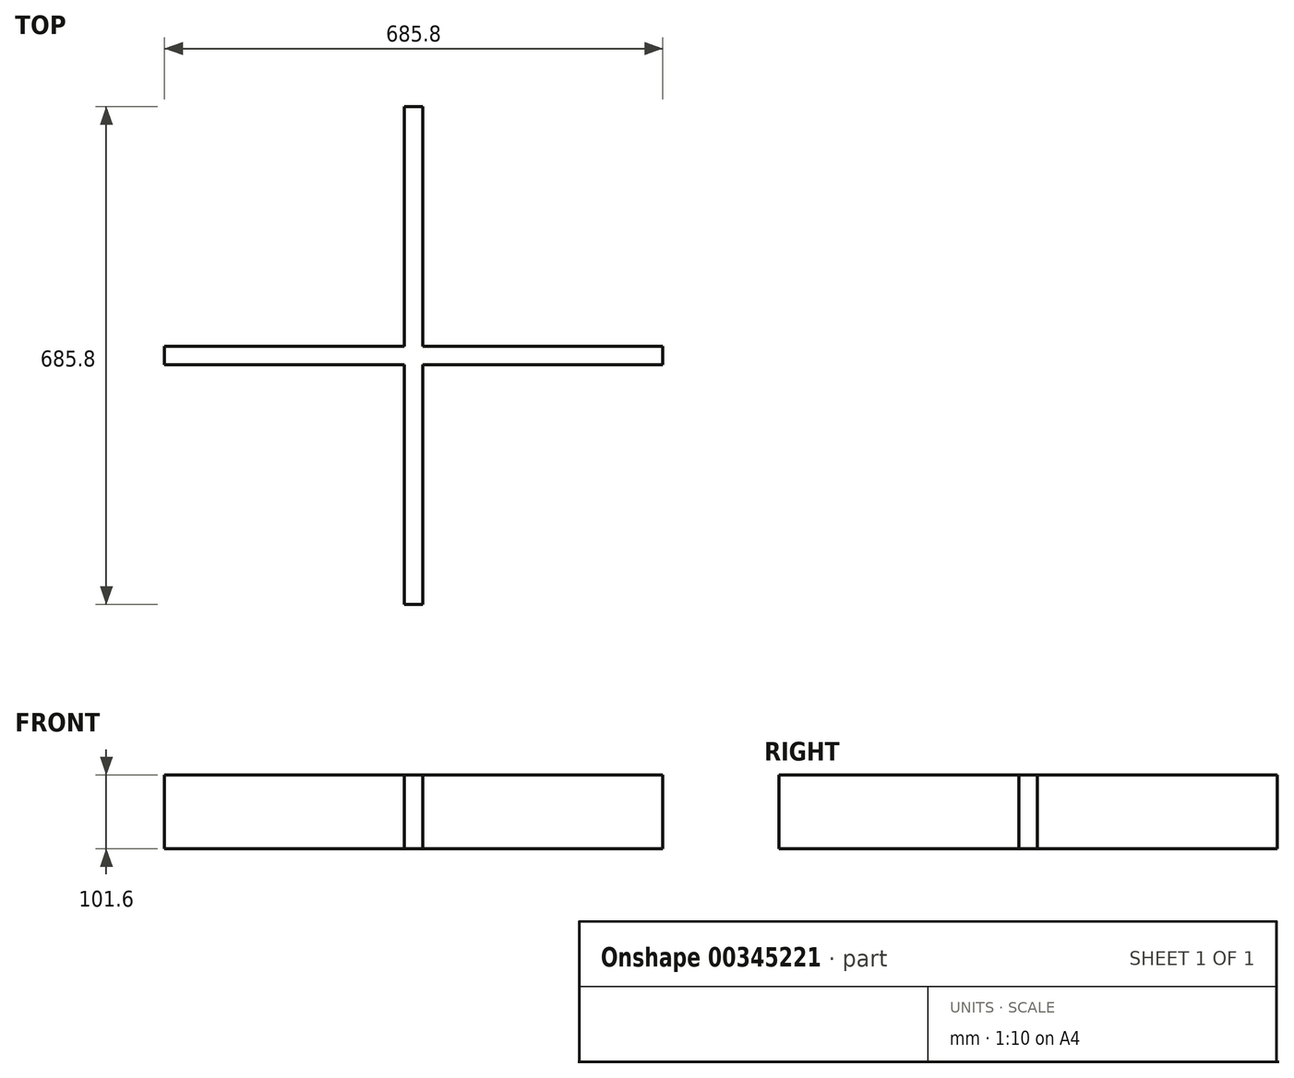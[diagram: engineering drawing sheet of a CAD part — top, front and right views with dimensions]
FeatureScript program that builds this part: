
annotation { "Feature Type Name" : "Feature", "Feature Type Description" : "" }
export const myFeature = defineFeature(function(context is Context, id is Id, definition is map)
    precondition{}
    {
        {
            var Q0;
            Q0=qCreatedBy(makeId("Top.planeOp"),FACE);
            var sketch = newSketch(context, id + "F0", { "sketchPlane" : qUnion([Q0])});
            skLineSegment(sketch, "E0", {"start": v(-12.24, 338.18) * mm, "end": v(-12.24, 7.98) * mm});
            skLineSegment(sketch, "E1", {"start": v(-12.24, 7.98) * mm, "end": v(-342.44, 7.98) * mm});
            skLineSegment(sketch, "E2", {"start": v(-342.44, 7.98) * mm, "end": v(-342.44, -17.42) * mm});
            skLineSegment(sketch, "E3", {"start": v(-342.44, -17.42) * mm, "end": v(-12.24, -17.42) * mm});
            skLineSegment(sketch, "E4", {"start": v(-12.24, -17.42) * mm, "end": v(-12.24, -347.62) * mm});
            skLineSegment(sketch, "E5", {"start": v(-12.24, -347.62) * mm, "end": v(13.16, -347.62) * mm});
            skLineSegment(sketch, "E6", {"start": v(13.16, -347.62) * mm, "end": v(13.16, -17.42) * mm});
            skLineSegment(sketch, "E7", {"start": v(13.16, -17.42) * mm, "end": v(343.36, -17.42) * mm});
            skLineSegment(sketch, "E8", {"start": v(343.36, -17.42) * mm, "end": v(343.36, 7.98) * mm});
            skLineSegment(sketch, "E9", {"start": v(343.36, 7.98) * mm, "end": v(13.16, 7.98) * mm});
            skLineSegment(sketch, "E10", {"start": v(13.16, 7.98) * mm, "end": v(13.16, 338.18) * mm});
            skLineSegment(sketch, "E11", {"start": v(13.16, 338.18) * mm, "end": v(-12.24, 338.18) * mm});
            skSolve(sketch);
        }
        {
            var Q0;
            Q0=makeQuery(id+"F0.imprint","IMPRINT",FACE,{"disambiguationData":[TD([[makeQuery(id+"F0.imprint","IMPRINT",EDGE,{"derivedFrom":sQuery(id+"F0.wireOp",EDGE,"E0")}),1.0]])]});
            extrude(context, id + "F1", {"entities" : qUnion([Q0]), "depth" : 101.6 * mm});
        }
    });
